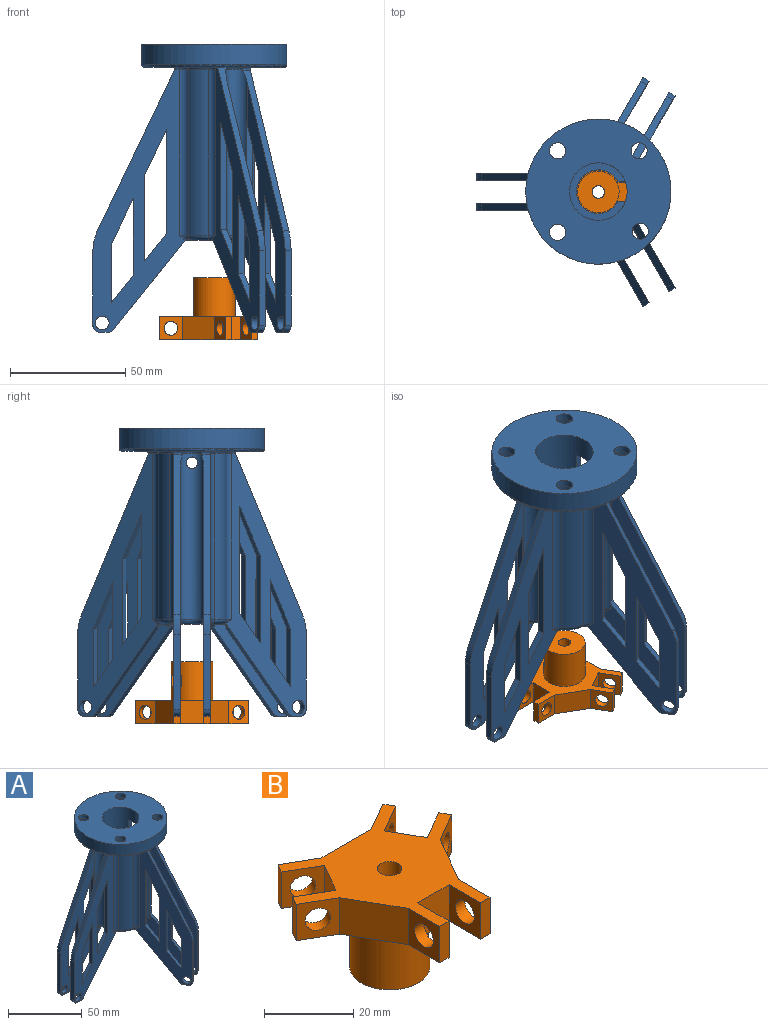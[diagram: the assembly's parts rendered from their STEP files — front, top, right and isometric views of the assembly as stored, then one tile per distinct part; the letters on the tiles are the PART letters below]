
ASSEMBLY  parts=2 mates=1
PART A: 223 faces, bbox 87.4x99.9x125.6 mm
  f0: plane 33.87x2.6mm, normal (0.5,-0.87,0), area 101.6mm2, adj f3,f28,f65,f111
  f1: plane 33.87x2.6mm, normal (0.5,-0.87,0), area 101.6mm2, adj f6,f27,f55,f112
  f2: plane 38.03x2.6mm, normal (-0.5,0.87,0), area 114.1mm2, adj f4,f28,f65,f109
  f3: plane 21.22x10.33mm, normal (-0.45,0.78,-0.43), area 70.6mm2, adj f0,f28,f65,f108
  f4: plane 12.74x10.33mm, normal (0.39,-0.68,0.62), area 48.9mm2, adj f2,f28,f65,f110,f139
  f5: plane 12.74x10.35mm, normal (0.39,-0.68,0.62), area 48.9mm2, adj f27,f55,f113,f139,f222
  f6: plane 21.22x10.33mm, normal (-0.45,0.78,-0.43), area 70.6mm2, adj f1,f27,f55,f115
  f7: plane 33.3x3mm, normal (-1,0,0), area 99.9mm2, adj f17,f32,f33,f101
  f8: plane 33.3x3mm, normal (-1,0,0), area 99.9mm2, adj f18,f30,f31,f106
  f9: plane 37.46x3mm, normal (1,0,0), area 112.4mm2, adj f16,f32,f33,f103
  f10: plane 33.3x2.6mm, normal (0.5,0.87,0), area 99.9mm2, adj f12,f23,f25,f94
  f11: plane 37.46x2.6mm, normal (-0.5,-0.87,0), area 112.4mm2, adj f13,f23,f25,f92
  f12: plane 19.8x9.73mm, normal (-0.45,-0.78,-0.43), area 65.9mm2, adj f10,f23,f25,f95
  f13: plane 11.88x9.73mm, normal (0.39,0.68,0.62), area 45.6mm2, adj f11,f23,f25,f93
  f14: plane 11.88x9.73mm, normal (0.39,0.68,0.62), area 45.6mm2, adj f22,f24,f98,f221
  f15: plane 19.8x9.73mm, normal (-0.45,-0.78,-0.43), area 65.9mm2, adj f22,f24,f96,f220
  f16: plane 19.8x9.51mm, normal (0.9,0,-0.43), area 65.9mm2, adj f9,f32,f33,f102
  f17: plane 11.88x9.51mm, normal (-0.78,0,0.62), area 45.6mm2, adj f7,f32,f33,f100
  f18: plane 11.88x9.51mm, normal (-0.78,0,0.62), area 45.6mm2, adj f8,f30,f31,f107
  f19: plane 19.8x9.51mm, normal (0.9,0,-0.43), area 65.9mm2, adj f30,f31,f105,f219
  f20: plane 61x49.87mm, normal (0,0,-1), area 1121.1mm2, adj f91,f118,f148,f149,f150,f151,f152,f153
  f21: cylinder r=9.5mm len=58mm, axis (0,0,1), area 2950.9mm2, adj f39,f62,f63,f117
  f22: plane 114.46x35.18mm, normal (-0.87,0.5,0), area 1718.5mm2, adj f14,f15,f38,f39,f69,f74,f78,f79
  f23: plane 114.64x37.41mm, normal (0.87,-0.5,0), area 1902.9mm2, adj f10,f11,f12,f13,f39,f60,f61,f67
  f24: plane 108.1x33.39mm, normal (0.87,-0.5,0), area 1368mm2, adj f14,f15,f38,f68,f69,f74,f78,f79
  f25: plane 108.1x33.39mm, normal (-0.87,0.5,0), area 1368mm2, adj f10,f11,f12,f13,f60,f66,f67,f75
  f26: plane 32.45x2.6mm, normal (0.5,-0.87,0), area 97.3mm2, adj f28,f65,f121,f136
  f27: plane 114.58x37.3mm, normal (-0.87,-0.5,0), area 1659.6mm2, adj f1,f5,f6,f39,f56,f71,f87,f90
  f28: plane 114.59x37.32mm, normal (0.87,0.5,0), area 1659.6mm2, adj f0,f2,f3,f4,f26,f39,f73,f86
  f29: plane 32.45x3mm, normal (-1,0,0), area 97.3mm2, adj f32,f33,f123,f134
  f30: plane 114x40.09mm, normal (0,-1,0), area 1718.5mm2, adj f8,f18,f19,f37,f39,f58,f80,f84
  f31: plane 108.1x38.56mm, normal (0,1,0), area 1368mm2, adj f8,f18,f19,f36,f37,f58,f80,f84
  f32: plane 108.1x38.56mm, normal (0,-1,0), area 1368mm2, adj f7,f9,f16,f17,f29,f34,f35,f81
  f33: plane 114.46x40.55mm, normal (0,1,0), area 1718.5mm2, adj f7,f9,f16,f17,f29,f35,f39,f81
  f34: cylinder r=15mm len=1.56mm, axis (0,0,1), area 0.7mm2, adj f32,f81,f202
  f35: plane 3.56x3mm, normal (0,0,-1), area 10.7mm2, adj f32,f33,f129,f134
  f36: cylinder r=15mm len=1.56mm, axis (0,0,1), area 0.7mm2, adj f31,f80,f200
  f37: plane 3.56x3mm, normal (0,0,-1), area 10.7mm2, adj f30,f31,f128,f133
  f38: plane 32.45x2.6mm, normal (0.5,0.87,0), area 97.3mm2, adj f22,f24,f125,f132
  f39: plane 31.01x27.98mm, normal (0,0,-1), area 268.4mm2, adj f21,f22,f23,f27,f28,f30,f33,f55
  f40: cylinder r=3.5mm len=7mm, axis (0,0,-1), area 66mm2, adj f45,f50
  f41: cylinder r=3.5mm len=7mm, axis (0,0,-1), area 66mm2, adj f45,f48
  f42: cylinder r=3.5mm len=7mm, axis (0,0,-1), area 66mm2, adj f45,f52
  f43: cylinder r=31.5mm len=63mm, axis (0,0,-1), area 1781.3mm2, adj f45,f118
  f44: cylinder r=3.5mm len=7mm, axis (0,0,-1), area 66mm2, adj f45,f54
  f45: plane 63x63mm, normal (0,0,1), area 2472.4mm2, adj f40,f41,f42,f43,f44,f116
  f46: plane 36.71x18.74mm, normal (0,0,-1), area 394mm2, adj f62,f63,f116,f118,f146,f147,f165,f167
  f47: cylinder r=5.5mm len=11mm, axis (0,0,-1), area 210.8mm2, adj f48,f184,f185,f186
  f48: plane 11x11mm, normal (0,0,-1), area 56.5mm2, adj f41,f47
  f49: cylinder r=5.5mm len=11mm, axis (0,0,-1), area 210.3mm2, adj f50,f169,f170,f171,f172,f173,f174
  f50: plane 11x11mm, normal (0,0,-1), area 56.5mm2, adj f40,f49
  f51: cylinder r=5.5mm len=11mm, axis (0,0,-1), area 210.8mm2, adj f52,f175,f176,f177
  f52: plane 11x11mm, normal (0,0,-1), area 56.5mm2, adj f42,f51
  f53: cylinder r=5.5mm len=11mm, axis (0,0,-1), area 211.1mm2, adj f54,f178,f179,f180,f181,f182,f183
  f54: plane 11x11mm, normal (0,0,-1), area 56.5mm2, adj f44,f53
  f55: plane 108.68x34.9mm, normal (0.87,0.5,0), area 1343mm2, adj f1,f5,f6,f39,f56,f70,f71,f87
  f56: plane 32.45x2.6mm, normal (0.5,-0.87,0), area 97.3mm2, adj f27,f55,f120,f137
  f57: cylinder r=15mm len=72mm, axis (0,0,1), area 733.6mm2, adj f141,f142,f161,f191
  f58: plane 32.45x3mm, normal (-1,0,0), area 97.3mm2, adj f30,f31,f122,f133
  f59: cylinder r=15mm len=72mm, axis (0,0,1), area 733.6mm2, adj f144,f145,f153,f188
  f60: plane 32.45x2.6mm, normal (0.5,0.87,0), area 97.3mm2, adj f23,f25,f124,f135
  f61: cylinder r=15mm len=72mm, axis (0,0,1), area 213.2mm2, adj f23,f62,f146,f198
  f62: plane 75.31x7.24mm, normal (0,-1,0), area 385.6mm2, adj f21,f39,f46,f61,f116,f117,f146,f198
  f63: plane 75.11x7.04mm, normal (0,1,0), area 385.6mm2, adj f21,f39,f46,f64,f116,f117,f165,f193
  f64: cylinder r=15mm len=72mm, axis (0,0,1), area 56.5mm2, adj f63,f138,f165,f193
  f65: plane 108.68x34.9mm, normal (-0.87,-0.5,0), area 1343mm2, adj f0,f2,f3,f4,f26,f39,f72,f73
  f66: cylinder r=15mm len=1.35mm, axis (0,0,1), area 0.7mm2, adj f25,f75,f208
  f67: plane 4.58x4.38mm, normal (0,0,-1), area 10.7mm2, adj f23,f25,f130,f135
  f68: cylinder r=15mm len=1.68mm, axis (0,0,1), area 0.7mm2, adj f24,f74,f205
  f69: plane 4.58x4.38mm, normal (0,0,-1), area 10.7mm2, adj f22,f24,f131,f132
  f70: cylinder r=15mm len=1.68mm, axis (0,0,1), area 0.7mm2, adj f55,f87,f218
  f71: plane 4.58x4.38mm, normal (0,0,-1), area 10.7mm2, adj f27,f55,f126,f137
  f72: cylinder r=15mm len=1.35mm, axis (0,0,1), area 0.7mm2, adj f65,f86,f217
  f73: plane 4.58x4.38mm, normal (0,0,-1), area 10.7mm2, adj f28,f65,f127,f136
  f74: plane 38.93x28.04mm, normal (-0.39,-0.68,-0.62), area 146.1mm2, adj f22,f24,f39,f68,f131,f205
  f75: plane 38.93x28.5mm, normal (-0.39,-0.68,-0.62), area 146.1mm2, adj f23,f25,f39,f66,f130,f208
  f76: cylinder r=3mm len=6.7mm, axis (0.87,-0.5,0), area 56.5mm2, adj f23,f25
  f77: plane 69.68x30.6mm, normal (0.45,0.78,0.43), area 232.6mm2, adj f23,f25,f124,f140,f148
  f78: cylinder r=3mm len=6.7mm, axis (0.87,-0.5,0), area 56.5mm2, adj f22,f24
  f79: plane 69.68x30.98mm, normal (0.45,0.78,0.43), area 232.6mm2, adj f22,f24,f125,f140,f150
  f80: plane 38.93x31.17mm, normal (0.78,0,-0.62), area 146.1mm2, adj f30,f31,f36,f39,f128,f200
  f81: plane 38.93x31.17mm, normal (0.78,0,-0.62), area 146.1mm2, adj f32,f33,f34,f39,f129,f202
  f82: cylinder r=3mm len=6mm, axis (0,-1,0), area 56.5mm2, adj f32,f33
  f83: plane 69.68x33.57mm, normal (-0.9,0,0.43), area 232.6mm2, adj f32,f33,f123,f143,f156
  f84: cylinder r=3mm len=6mm, axis (0,-1,0), area 56.5mm2, adj f30,f31
  f85: plane 69.68x33.57mm, normal (-0.9,0,0.43), area 232.6mm2, adj f30,f31,f122,f143,f158
  f86: plane 38.93x28.5mm, normal (-0.39,0.68,-0.62), area 146.1mm2, adj f28,f39,f65,f72,f127,f217
  f87: plane 38.93x28.04mm, normal (-0.39,0.68,-0.62), area 146.1mm2, adj f27,f39,f55,f70,f126,f218
  f88: cylinder r=3mm len=6.7mm, axis (-0.87,-0.5,0), area 56.5mm2, adj f28,f65
  f89: plane 69.68x30.6mm, normal (0.45,-0.78,0.43), area 232.6mm2, adj f28,f65,f121,f139,f166
  f90: cylinder r=3mm len=6.7mm, axis (-0.87,-0.5,0), area 56.5mm2, adj f27,f55
  f91: plane 71.22x32.68mm, normal (0.45,-0.78,0.43), area 239.5mm2, adj f20,f27,f55,f120,f139,f163,f164
  f92: plane 19.8x9.73mm, normal (-0.45,-0.78,-0.43), area 65.9mm2, adj f11,f23,f25,f93
  f93: plane 45.38x2.6mm, normal (0.5,0.87,0), area 136.1mm2, adj f13,f23,f25,f92
  f94: plane 11.88x9.73mm, normal (0.39,0.68,0.62), area 45.6mm2, adj f10,f23,f25,f95
  f95: plane 25.38x2.6mm, normal (-0.5,-0.87,0), area 76.1mm2, adj f12,f23,f25,f94
  f96: plane 25.38x2.6mm, normal (-0.5,-0.87,0), area 76.1mm2, adj f15,f22,f24,f97
  f97: plane 11.88x9.73mm, normal (0.39,0.68,0.62), area 45.6mm2, adj f22,f24,f96,f220
  f98: plane 45.38x2.6mm, normal (0.5,0.87,0), area 136.1mm2, adj f14,f22,f24,f99
  f99: plane 19.8x9.73mm, normal (-0.45,-0.78,-0.43), area 65.9mm2, adj f22,f24,f98,f221
  f100: plane 25.38x3mm, normal (1,0,0), area 76.1mm2, adj f17,f32,f33,f101
  f101: plane 19.8x9.51mm, normal (0.9,0,-0.43), area 65.9mm2, adj f7,f32,f33,f100
  f102: plane 45.38x3mm, normal (-1,0,0), area 136.1mm2, adj f16,f32,f33,f103
  f103: plane 11.88x9.51mm, normal (-0.78,0,0.62), area 45.6mm2, adj f9,f32,f33,f102
  f104: plane 11.88x9.51mm, normal (-0.78,0,0.62), area 45.6mm2, adj f30,f31,f105,f219
  f105: plane 45.38x3mm, normal (-1,0,0), area 136.1mm2, adj f19,f30,f31,f104
  f106: plane 19.8x9.51mm, normal (0.9,0,-0.43), area 65.9mm2, adj f8,f30,f31,f107
  f107: plane 25.38x3mm, normal (1,0,0), area 76.1mm2, adj f18,f30,f31,f106
  f108: plane 25.38x2.6mm, normal (-0.5,0.87,0), area 76.1mm2, adj f3,f28,f65,f111
  f109: plane 21.23x10.33mm, normal (-0.45,0.78,-0.43), area 70.7mm2, adj f2,f28,f65,f110,f139
  f110: plane 46.52x2.64mm, normal (0.5,-0.87,0), area 141.7mm2, adj f4,f28,f109,f139
  f111: plane 12.73x10.33mm, normal (0.39,-0.68,0.62), area 48.9mm2, adj f0,f28,f65,f108
  f112: plane 12.73x10.33mm, normal (0.39,-0.68,0.62), area 48.9mm2, adj f1,f27,f55,f115
  f113: plane 46.52x2.64mm, normal (0.5,-0.87,0), area 141.7mm2, adj f5,f27,f114,f139
  f114: plane 21.23x10.35mm, normal (-0.45,0.78,-0.43), area 70.7mm2, adj f27,f55,f113,f139,f222
  f115: plane 25.38x2.6mm, normal (-0.5,0.87,0), area 76.1mm2, adj f6,f27,f55,f112
  f116: cylinder r=12.5mm len=27mm, axis (0,0,1), area 1953.3mm2, adj f45,f46,f62,f63,f117,f119
  f117: plane 25x24.26mm, normal (0,0,1), area 181.1mm2, adj f21,f62,f63,f116
  f118: torus R=30.5mm, axis (0,0,1), area 307.3mm2, adj f20,f43,f46,f169,f174,f175,f177,f178
  f119: cylinder r=2.5mm len=5mm, axis (1,0,0), area 39.3mm2, adj f116,f143
  f120: cylinder r=20mm len=8.66mm, axis (-0.87,-0.5,0), area 26.9mm2, adj f27,f55,f56,f91
  f121: cylinder r=20mm len=8.66mm, axis (0.87,0.5,0), area 26.9mm2, adj f26,f28,f65,f89
  f122: cylinder r=20mm len=8.66mm, axis (0,-1,0), area 26.9mm2, adj f30,f31,f58,f85
  f123: cylinder r=20mm len=8.66mm, axis (0,1,0), area 26.9mm2, adj f29,f32,f33,f83
  f124: cylinder r=20mm len=8.66mm, axis (0.87,-0.5,0), area 26.9mm2, adj f23,f25,f60,f77
  f125: cylinder r=20mm len=8.66mm, axis (-0.87,0.5,0), area 26.9mm2, adj f22,f24,f38,f79
  f126: cylinder r=3mm len=3.77mm, axis (0.87,0.5,0), area 8.1mm2, adj f27,f55,f71,f87
  f127: cylinder r=3mm len=3.77mm, axis (0.87,0.5,0), area 8.1mm2, adj f28,f65,f73,f86
  f128: cylinder r=3mm len=3mm, axis (0,-1,0), area 8.1mm2, adj f30,f31,f37,f80
  f129: cylinder r=3mm len=3mm, axis (0,-1,0), area 8.1mm2, adj f32,f33,f35,f81
  f130: cylinder r=3mm len=3.77mm, axis (-0.87,0.5,0), area 8.1mm2, adj f23,f25,f67,f75
  f131: cylinder r=3mm len=3.77mm, axis (-0.87,0.5,0), area 8.1mm2, adj f22,f24,f69,f74
  f132: cylinder r=3mm len=4.1mm, axis (-0.87,0.5,0), area 14.1mm2, adj f22,f24,f38,f69
  f133: cylinder r=3mm len=3mm, axis (0,-1,0), area 14.1mm2, adj f30,f31,f37,f58
  f134: cylinder r=3mm len=3mm, axis (0,-1,0), area 14.1mm2, adj f29,f32,f33,f35
  f135: cylinder r=3mm len=4.1mm, axis (-0.87,0.5,0), area 14.1mm2, adj f23,f25,f60,f67
  f136: cylinder r=3mm len=4.1mm, axis (0.87,0.5,0), area 14.1mm2, adj f26,f28,f65,f73
  f137: cylinder r=3mm len=4.1mm, axis (0.87,0.5,0), area 14.1mm2, adj f27,f55,f56,f71
  f138: cylinder r=5mm len=72mm, axis (0,0,1), area 310.8mm2, adj f28,f64,f167,f194
  f139: cylinder r=5mm len=72mm, axis (0,0,1), area 1050.1mm2, adj f4,f5,f55,f65,f89,f91,f109,f110
  f140: cylinder r=5mm len=72mm, axis (0,0,1), area 1113.4mm2, adj f24,f25,f77,f79,f148,f149,f150,f196
  f141: cylinder r=5mm len=72mm, axis (0,0,1), area 310.8mm2, adj f27,f57,f162,f192
  f142: cylinder r=5mm len=72mm, axis (0,0,1), area 310.8mm2, adj f30,f57,f160,f190
  f143: cylinder r=5mm len=72mm, axis (0,0,1), area 1093.1mm2, adj f31,f32,f83,f85,f119,f156,f157,f158
  f144: cylinder r=5mm len=72mm, axis (0,0,1), area 310.8mm2, adj f33,f59,f154,f189
  f145: cylinder r=5mm len=72mm, axis (0,0,1), area 310.8mm2, adj f22,f59,f152,f187
  f146: torus R=16mm, axis (0,0,1), area 4.6mm2, adj f46,f61,f62,f147
  f147: cylinder r=1mm len=5.24mm, axis (0.5,0.87,0), area 7.4mm2, adj f23,f46,f146,f148,f171
  f148: cylinder r=1mm len=5.02mm, axis (-0.87,0.5,0), area 7.4mm2, adj f20,f23,f77,f140,f147,f149,f171,f172
  f149: torus R=4mm, axis (0,0,1), area 15.4mm2, adj f20,f140,f148,f150
  f150: cylinder r=1mm len=5.17mm, axis (-0.87,0.5,0), area 8.9mm2, adj f20,f22,f79,f140,f149,f151
  f151: cylinder r=1mm len=3.17mm, axis (-0.5,-0.87,0), area 4.1mm2, adj f20,f22,f150,f152
  f152: torus R=4mm, axis (0,0,1), area 6.3mm2, adj f20,f145,f151,f153
  f153: torus R=16mm, axis (0,0,1), area 16.4mm2, adj f20,f59,f152,f154
  f154: torus R=4mm, axis (0,0,1), area 6.3mm2, adj f20,f144,f153,f155
  f155: cylinder r=1mm len=3.08mm, axis (-1,0,0), area 4.1mm2, adj f20,f33,f154,f156
  f156: cylinder r=1mm len=5.39mm, axis (0,-1,0), area 8.9mm2, adj f20,f33,f83,f143,f155,f157
  f157: torus R=4mm, axis (0,0,1), area 15.4mm2, adj f20,f143,f156,f158
  f158: cylinder r=1mm len=5.39mm, axis (0,-1,0), area 8.9mm2, adj f20,f30,f85,f143,f157,f159
  f159: cylinder r=1mm len=3.08mm, axis (1,0,0), area 4.1mm2, adj f20,f30,f158,f160
  f160: torus R=4mm, axis (0,0,1), area 6.3mm2, adj f20,f142,f159,f161
  f161: torus R=16mm, axis (0,0,1), area 16.4mm2, adj f20,f57,f160,f162
  f162: torus R=4mm, axis (0,0,1), area 6.3mm2, adj f20,f141,f161,f163
  f163: cylinder r=1mm len=2.21mm, axis (0.5,-0.87,0), area 2.7mm2, adj f20,f27,f91,f162
  f164: torus R=4mm, axis (0,0,1), area 13.5mm2, adj f20,f91,f139,f166
  f165: torus R=16mm, axis (0,0,1), area 1.5mm2, adj f46,f63,f64,f167
  f166: cylinder r=1mm len=4.69mm, axis (0.87,0.5,0), area 7.1mm2, adj f20,f28,f89,f139,f164,f168,f180,f181
  f167: torus R=4mm, axis (0,0,1), area 6.3mm2, adj f46,f138,f165,f168
  f168: cylinder r=1mm len=2.69mm, axis (-0.5,0.87,0), area 3.6mm2, adj f28,f46,f166,f167,f181
  f169: bspline ~3.46x2.8mm, area 1.8mm2, adj f49,f118,f170
  f170: torus R=6.5mm, axis (0,0,1), area 17.1mm2, adj f46,f49,f169,f171
  f171: bspline ~1.26x1.23mm, area 0.2mm2, adj f49,f147,f148,f170,f172
  f172: bspline ~5.49x3.62mm, area 6.4mm2, adj f49,f148,f171,f173
  f173: torus R=6.5mm, axis (0,0,1), area 21.5mm2, adj f20,f49,f172,f174
  f174: bspline ~3.46x2.8mm, area 1.8mm2, adj f49,f118,f173
  f175: bspline ~3.46x2.8mm, area 1.8mm2, adj f51,f118,f176
  f176: torus R=6.5mm, axis (0,0,1), area 46.3mm2, adj f20,f51,f175,f177
  f177: bspline ~3.46x2.8mm, area 1.8mm2, adj f51,f118,f176
  f178: bspline ~2.98x2.61mm, area 1.7mm2, adj f53,f118,f179
  f179: torus R=6.5mm, axis (0,0,1), area 21.1mm2, adj f20,f53,f178,f180
  f180: bspline ~5.09x4.01mm, area 5.1mm2, adj f53,f166,f179,f181
  f181: bspline ~1.51x1.5mm, area 1.1mm2, adj f53,f166,f168,f180,f182
  f182: torus R=6.5mm, axis (0,0,1), area 17.8mm2, adj f46,f53,f181,f183
  f183: bspline ~3.51x2.71mm, area 1.8mm2, adj f53,f118,f182
  f184: bspline ~3.46x2.8mm, area 1.8mm2, adj f47,f118,f185
  f185: torus R=6.5mm, axis (0,0,1), area 46.3mm2, adj f20,f47,f184,f186
  f186: bspline ~3.46x2.8mm, area 1.8mm2, adj f47,f118,f185
  f187: torus R=7mm, axis (0,0,-1), area 6.2mm2, adj f39,f145,f188,f213,f214
  f188: torus R=13mm, axis (0,0,-1), area 30.5mm2, adj f39,f59,f187,f189
  f189: torus R=7mm, axis (0,0,-1), area 6.2mm2, adj f39,f144,f188,f215,f216
  f190: torus R=7mm, axis (0,0,-1), area 6.2mm2, adj f39,f142,f191,f211,f212
  f191: torus R=13mm, axis (0,0,-1), area 30.5mm2, adj f39,f57,f190,f192
  f192: torus R=7mm, axis (0,0,-1), area 8.1mm2, adj f27,f39,f141,f191
  f193: torus R=13mm, axis (0,0,-1), area 1.7mm2, adj f39,f63,f64,f194
  f194: torus R=7mm, axis (0,0,-1), area 8.1mm2, adj f28,f39,f138,f193
  f195: torus R=7mm, axis (0,0,-1), area 38.2mm2, adj f39,f143,f199,f203
  f196: torus R=7mm, axis (0,0,-1), area 38.2mm2, adj f39,f140,f207,f210
  f197: torus R=7mm, axis (0,0,-1), area 41.7mm2, adj f39,f55,f65,f139
  f198: torus R=13mm, axis (0,0,-1), area 5.7mm2, adj f23,f39,f61,f62
  f199: bspline ~6.76x3mm, area 3.5mm2, adj f31,f195,f201
  f200: torus R=14mm, axis (0,0,-1), area 3.8mm2, adj f36,f39,f80,f201
  f201: cylinder r=1mm len=1mm, axis (-1,0,0), area 0.6mm2, adj f31,f39,f199,f200
  f202: torus R=14mm, axis (0,0,-1), area 3.8mm2, adj f34,f39,f81,f204
  f203: bspline ~6.76x3mm, area 3.5mm2, adj f32,f195,f204
  f204: cylinder r=1mm len=1mm, axis (1,0,0), area 0.6mm2, adj f32,f39,f202,f203
  f205: torus R=14mm, axis (0,0,-1), area 3.8mm2, adj f39,f68,f74,f206
  f206: cylinder r=1mm len=1.29mm, axis (0.5,0.87,0), area 0.6mm2, adj f24,f39,f205,f207
  f207: bspline ~5.48x3mm, area 3.5mm2, adj f24,f196,f206
  f208: torus R=14mm, axis (0,0,-1), area 3.8mm2, adj f39,f66,f75,f209
  f209: cylinder r=1mm len=1.29mm, axis (-0.5,-0.87,0), area 0.6mm2, adj f25,f39,f208,f210
  f210: bspline ~4.98x3.74mm, area 3.5mm2, adj f25,f196,f209
  f211: bspline ~3.83x2.47mm, area 1mm2, adj f30,f190,f212
  f212: bspline ~2.69x0.81mm, area 0.7mm2, adj f39,f190,f211
  f213: bspline ~3.22x2.47mm, area 1mm2, adj f22,f187,f214
  f214: bspline ~2.57x1.52mm, area 0.7mm2, adj f39,f187,f213
  f215: bspline ~2.69x0.81mm, area 0.7mm2, adj f39,f189,f216
  f216: bspline ~3.91x2.51mm, area 1mm2, adj f33,f189,f215
  f217: torus R=14mm, axis (0,0,-1), area 2.9mm2, adj f39,f65,f72,f86
  f218: torus R=14mm, axis (0,0,-1), area 2.9mm2, adj f39,f55,f70,f87
  f219: plane 37.46x3mm, normal (1,0,0), area 112.4mm2, adj f19,f30,f31,f104
  f220: plane 33.3x2.6mm, normal (0.5,0.87,0), area 99.9mm2, adj f15,f22,f24,f97
  f221: plane 37.46x2.6mm, normal (-0.5,-0.87,0), area 112.4mm2, adj f14,f22,f24,f99
  f222: plane 38.03x2.6mm, normal (-0.5,0.87,0), area 114.1mm2, adj f5,f27,f55,f114
PART B: 45 faces, bbox 49.3x42.7x27 mm
  f0: cylinder r=9mm len=18mm, axis (0,0,-1), area 917.5mm2, adj f1,f2,f5,f34,f41,f42
  f1: plane 10.25x9mm, normal (0,0,-1), area 42.4mm2, adj f0,f2,f5,f6,f7
  f2: plane 9x5.8mm, normal (-0.5,-0.87,0), area 54.9mm2, adj f0,f1,f3,f7,f8,f41
  f3: plane 5.8x4.38mm, normal (0.5,-0.87,0), area 29.3mm2, adj f2,f4,f8,f41
  f4: plane 5.8x5.05mm, normal (1,0,0), area 29.3mm2, adj f3,f5,f8,f41
  f5: plane 9x5.8mm, normal (0.5,0.87,0), area 54.9mm2, adj f0,f1,f4,f6,f8,f41
  f6: plane 4.38x2.53mm, normal (-0.5,0.87,0), area 5.1mm2, adj f1,f5,f7,f8
  f7: plane 5.05x1mm, normal (-1,0,0), area 5.1mm2, adj f1,f2,f6,f8
  f8: plane 10.1x8.75mm, normal (0,0,-1), area 42.5mm2, adj f2,f3,f4,f5,f6,f7,f44
  f9: plane 10x8.66mm, normal (-0.5,0.87,0), area 71.7mm2, adj f10,f32,f33,f34,f37
  f10: plane 16x10mm, normal (0,1,0), area 160mm2, adj f9,f11,f33,f34
  f11: plane 10x8.66mm, normal (0.5,0.87,0), area 71.7mm2, adj f10,f12,f33,f34,f40
  f12: plane 10x2.6mm, normal (-0.87,0.5,0), area 30mm2, adj f11,f13,f33,f34
  f13: plane 10x8.66mm, normal (-0.5,-0.87,0), area 71.7mm2, adj f12,f14,f33,f34,f40
  f14: plane 10x8.66mm, normal (-0.87,0.5,0), area 100mm2, adj f13,f15,f33,f34
  f15: plane 10x8.66mm, normal (0.5,0.87,0), area 71.7mm2, adj f14,f16,f33,f34,f39
  f16: plane 10x2.6mm, normal (-0.87,0.5,0), area 30mm2, adj f15,f17,f33,f34
  f17: plane 10x8.66mm, normal (-0.5,-0.87,0), area 71.7mm2, adj f16,f18,f33,f34,f39
  f18: plane 13.86x10mm, normal (-0.87,-0.5,0), area 160mm2, adj f17,f19,f33,f34
  f19: plane 10x10mm, normal (-1,0,0), area 71.7mm2, adj f18,f20,f33,f34,f36
  f20: plane 10x3mm, normal (0,-1,0), area 30mm2, adj f19,f21,f33,f34
  f21: plane 10x10mm, normal (1,0,0), area 71.7mm2, adj f20,f22,f33,f34,f36
  f22: plane 10x10mm, normal (0,-1,0), area 100mm2, adj f21,f23,f33,f34
  f23: plane 10x10mm, normal (-1,0,0), area 71.7mm2, adj f22,f24,f33,f34,f35
  f24: plane 10x3mm, normal (0,-1,0), area 30mm2, adj f23,f25,f33,f34
  f25: plane 10x10mm, normal (1,0,0), area 71.7mm2, adj f24,f26,f33,f34,f35
  f26: plane 13.86x10mm, normal (0.87,-0.5,0), area 160mm2, adj f25,f27,f33,f34
  f27: plane 10x8.66mm, normal (0.5,-0.87,0), area 71.7mm2, adj f26,f28,f33,f34,f38
  f28: plane 10x2.6mm, normal (0.87,0.5,0), area 30mm2, adj f27,f29,f33,f34
  f29: plane 10x8.66mm, normal (-0.5,0.87,0), area 71.7mm2, adj f28,f30,f33,f34,f38
  f30: plane 10x8.66mm, normal (0.87,0.5,0), area 100mm2, adj f29,f31,f33,f34
  f31: plane 10x8.66mm, normal (0.5,-0.87,0), area 71.7mm2, adj f30,f32,f33,f34,f37
  f32: plane 10x2.6mm, normal (0.87,0.5,0), area 30mm2, adj f9,f31,f33,f34
  f33: plane 49.32x42.71mm, normal (0,0,1), area 821.3mm2, adj f9,f10,f11,f12,f13,f14,f15,f16
  f34: plane 49.32x42.71mm, normal (0,0,-1), area 590.6mm2, adj f0,f9,f10,f11,f12,f13,f14,f15
  f35: cylinder r=3mm len=6mm, axis (1,0,0), area 56.5mm2, adj f23,f25
  f36: cylinder r=3mm len=6mm, axis (1,0,0), area 56.5mm2, adj f19,f21
  f37: cylinder r=3mm len=6.7mm, axis (-0.5,0.87,0), area 56.5mm2, adj f9,f31
  f38: cylinder r=3mm len=6.7mm, axis (-0.5,0.87,0), area 56.5mm2, adj f27,f29
  f39: cylinder r=3mm len=6.7mm, axis (0.5,0.87,0), area 56.5mm2, adj f15,f17
  f40: cylinder r=3mm len=6.7mm, axis (0.5,0.87,0), area 56.5mm2, adj f11,f13
  f41: plane 13.37x12.77mm, normal (0,0,1), area 84.9mm2, adj f0,f2,f3,f4,f5,f43
  f42: plane 18x18mm, normal (0,0,-1), area 230.7mm2, adj f0,f43
  f43: cylinder r=2.75mm len=6.2mm, axis (0,0,-1), area 107.1mm2, adj f41,f42
  f44: cylinder r=2.75mm len=15mm, axis (0,0,-1), area 259.2mm2, adj f8,f33
PLACE A at identity fixed
PLACE B rot(axis=(0.71,0.71,0),180deg) t=(0,0,-102.3)mm
MATE cylindrical B.f0 <-> A.f21  axis (0,0,1) through (0,0,-91.3)mm
